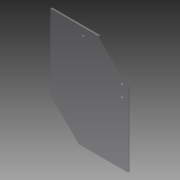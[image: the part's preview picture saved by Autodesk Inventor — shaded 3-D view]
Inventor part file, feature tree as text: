
AUTODESK INVENTOR PART (.ipt)
format: ipt  version: 2014 SP1 (Build 180222100, 222)  size: 77,312 bytes
history: native  units: in
note: dims shown in document units (in); Inventor stores cm internally (conversion verified against a paired STEP export)
features: reference x4, extrude x1, sketch x1
ambient origin geometry x8: Origin, YZ Plane, XZ Plane, XY Plane, X Axis, Y Axis, Z Axis, Center Point
bodies: Solid1 (feature_tree)
feature tree (6):
  extrude  "Extrusion1"  Depth=8.0in
  sketch  "Sketch1"  dims[d0=6.0in d1=8.0in d2=0.125in d3=0.0in]
  reference  "Reference1"
  reference  "Reference2"
  reference  "Reference3"
  reference  "Reference4"
